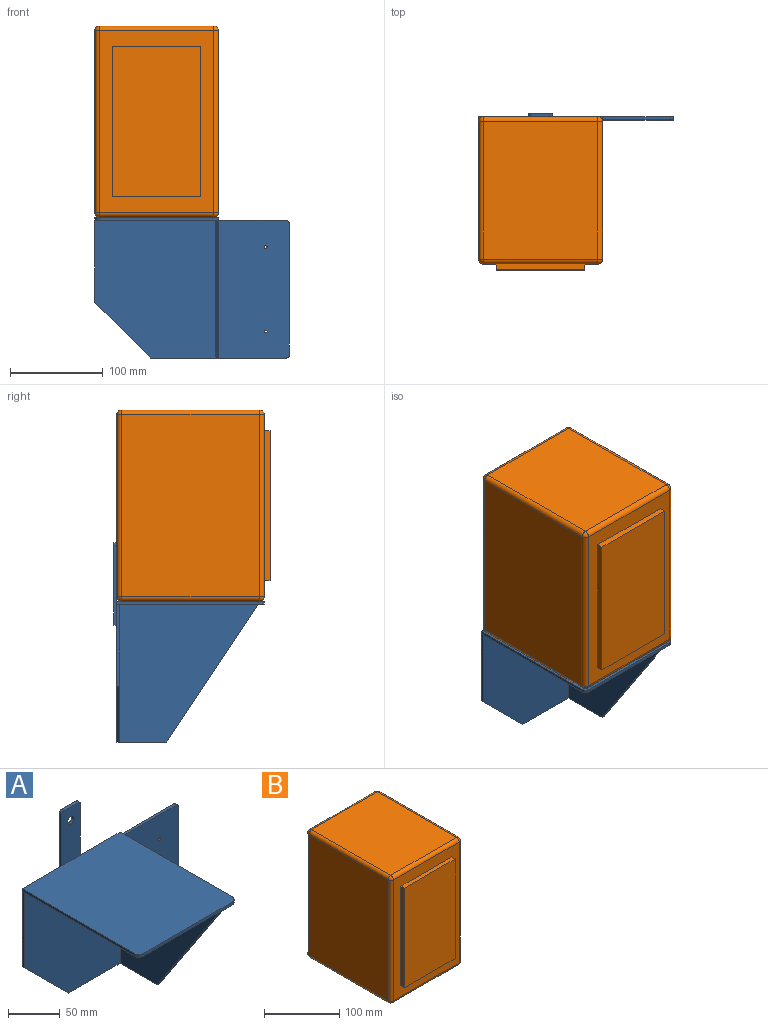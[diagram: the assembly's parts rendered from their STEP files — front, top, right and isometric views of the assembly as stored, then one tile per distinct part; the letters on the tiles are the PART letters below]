
ASSEMBLY  parts=2 mates=1
PART A: 30 faces, bbox 209.6x161.9x214.9 mm
  f0: plane 209.55x151.39mm, normal (0,1,0), area 29002.6mm2, adj f2,f6,f7,f8,f9,f10,f11,f12
  f1: plane 148.21x130.05mm, normal (0,-1,0), area 17480.3mm2, adj f2,f13,f14,f17,f20
  f2: plane 158.75x133.35mm, normal (0,0,-1), area 20255.2mm2, adj f0,f1,f3,f4,f5,f7,f17,f19
  f3: cylinder r=6.35mm len=6.35mm, axis (0,0,-1), area 31.7mm2, adj f2,f4,f7,f8
  f4: plane 120.65x3.18mm, normal (0,-1,0), area 383.1mm2, adj f2,f3,f5,f8
  f5: cylinder r=6.35mm len=6.35mm, axis (0,0,-1), area 31.7mm2, adj f2,f4,f6,f8
  f6: plane 152.4x151.39mm, normal (1,0,0), area 15306.8mm2, adj f0,f5,f8,f9,f13,f18,f19
  f7: plane 152.4x3.18mm, normal (-1,0,0), area 483.9mm2, adj f0,f2,f3,f8
  f8: plane 158.75x133.35mm, normal (0,0,1), area 21152mm2, adj f0,f3,f4,f5,f6,f7,f21
  f9: plane 73.03x3.18mm, normal (0,0,1), area 231.9mm2, adj f0,f6,f10,f18
  f10: cylinder r=3.17mm len=3.18mm, axis (0,1,0), area 15.8mm2, adj f0,f9,f11,f18
  f11: plane 141.86x3.18mm, normal (1,0,0), area 450.4mm2, adj f0,f10,f12,f18
  f12: cylinder r=3.17mm len=3.18mm, axis (0,1,0), area 15.8mm2, adj f0,f11,f13,f18
  f13: plane 146.34x53.98mm, normal (0,0,-1), area 625.9mm2, adj f0,f1,f6,f12,f14,f18,f19,f20
  f14: plane 59.91x59.91mm, normal (-0.71,0,-0.71), area 269mm2, adj f0,f1,f13,f17
  f15: cylinder r=1.59mm len=3.18mm, axis (0,1,0), area 31.7mm2, adj f0,f18
  f16: cylinder r=1.59mm len=3.18mm, axis (0,1,0), area 31.7mm2, adj f0,f18
  f17: plane 88.3x3.18mm, normal (-1,0,0), area 280.4mm2, adj f0,f1,f2,f14
  f18: plane 148.21x76.2mm, normal (0,-1,0), area 11273.5mm2, adj f6,f9,f10,f11,f12,f13,f15,f16
  f19: plane 148.21x98.43mm, normal (0,-0.83,-0.55), area 564.9mm2, adj f2,f6,f13,f20
  f20: plane 149.23x148.21mm, normal (-1,0,0), area 14823mm2, adj f1,f2,f13,f19
  f21: plane 63.5x25.4mm, normal (0,-1,0), area 1546.6mm2, adj f8,f22,f23,f24,f25,f26,f27
  f22: plane 85.73x3.18mm, normal (-1,0,0), area 272.2mm2, adj f0,f21,f23,f28,f29
  f23: cylinder r=3.17mm len=3.18mm, axis (0,-1,0), area 15.8mm2, adj f21,f22,f24,f29
  f24: plane 19.05x3.18mm, normal (0,0,1), area 60.5mm2, adj f21,f23,f25,f29
  f25: cylinder r=3.17mm len=3.18mm, axis (0,-1,0), area 15.8mm2, adj f21,f24,f26,f29
  f26: plane 85.73x3.18mm, normal (1,0,0), area 272.2mm2, adj f0,f21,f25,f28,f29
  f27: cylinder r=4.44mm len=8.88mm, axis (0,-1,0), area 88.6mm2, adj f21,f29
  f28: plane 25.4x3.18mm, normal (0,0,-1), area 80.6mm2, adj f0,f22,f26,f29
  f29: plane 88.9x25.4mm, normal (0,1,0), area 2191.8mm2, adj f22,f23,f24,f25,f26,f27,f28
PART B: 33 faces, bbox 133.4x165.1x206.4 mm
  f0: plane 196.22x123.19mm, normal (0,-1,0), area 8748.4mm2, adj f6,f7,f8,f9,f16,f25,f26,f30
  f1: plane 196.22x148.59mm, normal (-1,0,0), area 29155.6mm2, adj f19,f24,f27,f30
  f2: plane 196.22x148.59mm, normal (1,0,0), area 29155.6mm2, adj f11,f15,f16,f17
  f3: plane 196.22x123.19mm, normal (0,1,0), area 24140.1mm2, adj f11,f14,f18,f19,f31
  f4: plane 148.59x123.19mm, normal (0,0,1), area 18304.8mm2, adj f14,f15,f24,f25
  f5: plane 148.59x123.19mm, normal (0,0,-1), area 18304.8mm2, adj f17,f18,f26,f27
  f6: plane 161.93x6.35mm, normal (-1,0,0), area 1028.2mm2, adj f0,f7,f9,f10
  f7: plane 95.25x6.35mm, normal (0,0,-1), area 604.8mm2, adj f0,f6,f8,f10
  f8: plane 161.93x6.35mm, normal (1,0,0), area 1028.2mm2, adj f0,f7,f9,f10
  f9: plane 95.25x6.35mm, normal (0,0,1), area 604.8mm2, adj f0,f6,f8,f10
  f10: plane 161.93x95.25mm, normal (0,-1,0), area 15423.4mm2, adj f6,f7,f8,f9
  f11: cylinder r=5.08mm len=196.22mm, axis (0,0,-1), area 1565.7mm2, adj f2,f3,f12,f13
  f12: sphere r=5.08mm, area 40.5mm2, adj f11,f14,f15
  f13: sphere r=5.08mm, area 40.5mm2, adj f11,f17,f18
  f14: cylinder r=5.08mm len=123.19mm, axis (1,0,0), area 983mm2, adj f3,f4,f12,f20
  f15: cylinder r=5.08mm len=148.59mm, axis (0,-1,0), area 1185.7mm2, adj f2,f4,f12,f21
  f16: cylinder r=5.08mm len=196.22mm, axis (0,0,1), area 1565.7mm2, adj f0,f2,f21,f22
  f17: cylinder r=5.08mm len=148.59mm, axis (0,1,0), area 1185.7mm2, adj f2,f5,f13,f22
  f18: cylinder r=5.08mm len=123.19mm, axis (-1,0,0), area 983mm2, adj f3,f5,f13,f23
  f19: cylinder r=5.08mm len=196.22mm, axis (0,0,1), area 1565.7mm2, adj f1,f3,f20,f23
  f20: sphere r=5.08mm, area 40.5mm2, adj f14,f19,f24
  f21: sphere r=5.08mm, area 40.5mm2, adj f15,f16,f25
  f22: sphere r=5.08mm, area 40.5mm2, adj f16,f17,f26
  f23: sphere r=5.08mm, area 40.5mm2, adj f18,f19,f27
  f24: cylinder r=5.08mm len=148.59mm, axis (0,1,0), area 1185.7mm2, adj f1,f4,f20,f28
  f25: cylinder r=5.08mm len=123.19mm, axis (-1,0,0), area 983mm2, adj f0,f4,f21,f28
  f26: cylinder r=5.08mm len=123.19mm, axis (1,0,0), area 983mm2, adj f0,f5,f22,f29
  f27: cylinder r=5.08mm len=148.59mm, axis (0,-1,0), area 1185.7mm2, adj f1,f5,f23,f29
  f28: sphere r=5.08mm, area 40.5mm2, adj f24,f25,f30
  f29: sphere r=5.08mm, area 40.5mm2, adj f26,f27,f30
  f30: cylinder r=5.08mm len=196.22mm, axis (0,0,-1), area 1565.7mm2, adj f0,f1,f28,f29
  f31: cylinder r=3.17mm len=25.4mm, axis (0,1,0), area 506.7mm2, adj f3,f32
  f32: plane 6.35x6.35mm, normal (0,1,0), area 31.7mm2, adj f31
PLACE A t=(130.49,53.01,225.84)mm
PLACE B t=(130.49,53.08,229.02)mm
MATE fastened B.f5 <-> A.f8  axis (0,0,-1) through (130.49,53.08,229.02)mm
